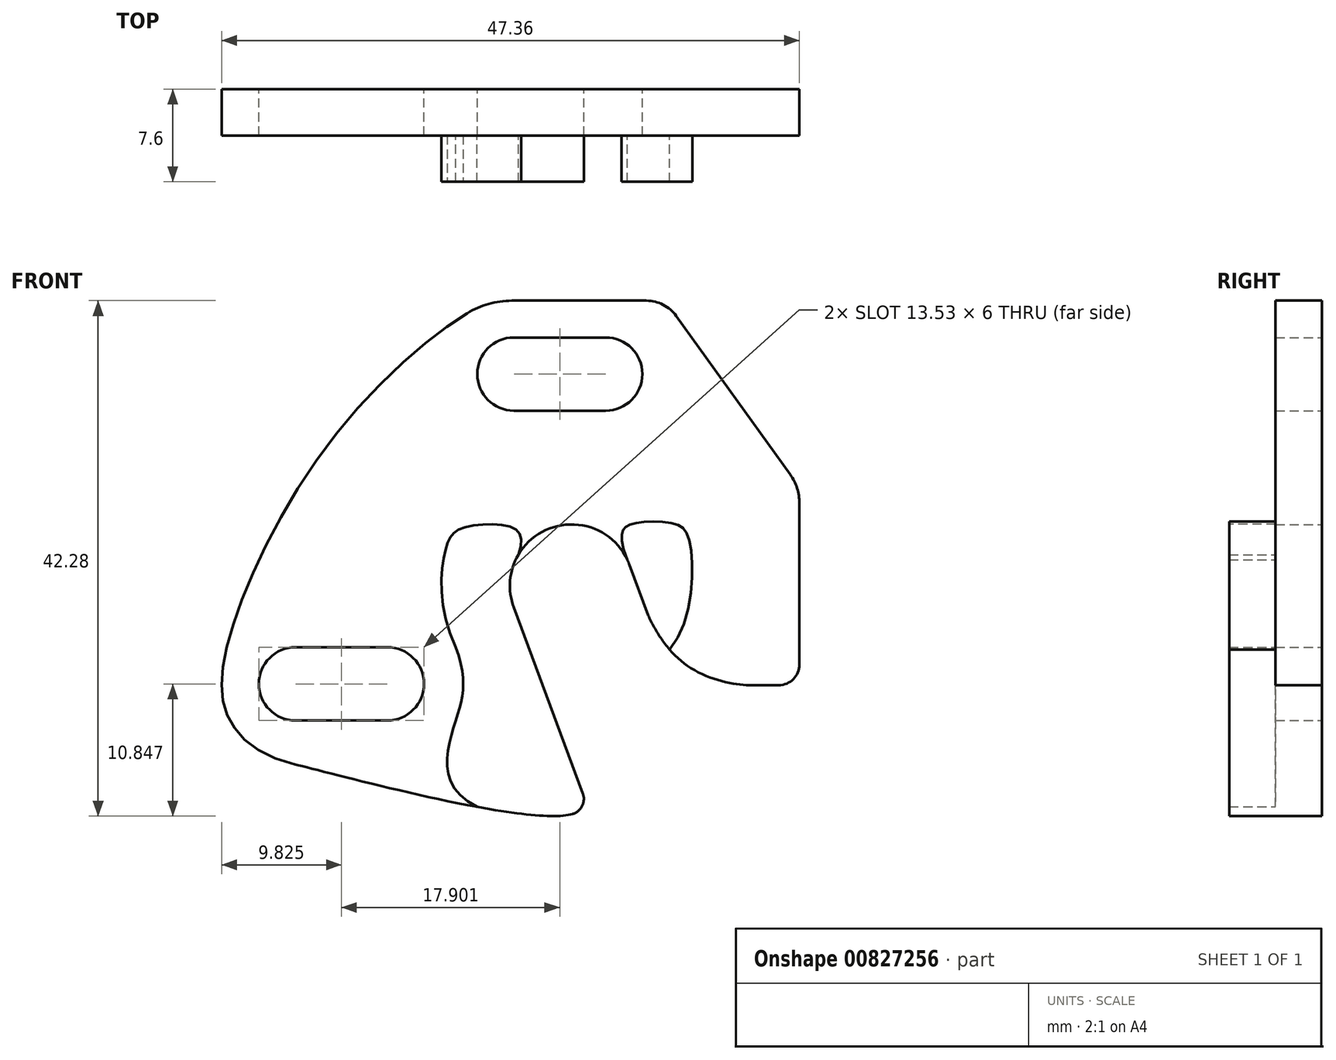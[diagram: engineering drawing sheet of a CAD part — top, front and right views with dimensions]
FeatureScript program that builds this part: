
annotation { "Feature Type Name" : "Feature", "Feature Type Description" : "" }
export const myFeature = defineFeature(function(context is Context, id is Id, definition is map)
    precondition{}
    {
        {
            var Q0;
            Q0=qCreatedBy(makeId("Front.planeOp"),FACE);
            var sketch = newSketch(context, id + "F0", { "sketchPlane" : qUnion([Q0])});
            skLineSegment(sketch, "E0", {"start": v(8.14, 19.75) * mm, "end": v(-6.15, 19.75) * mm});
            skLineSegment(sketch, "E1", {"start": v(8.14, 19.75) * mm, "end": v(19.14, 4.43) * mm});
            skLineSegment(sketch, "E2", {"start": v(19.14, 4.43) * mm, "end": v(19.14, -11.79) * mm});
            skFitSpline(sketch, "E3", {"points": [v(-6.15, 19.75) * mm, v(-18.96, 8.66) * mm, v(-27.78, -8.68) * mm, v(-27.55, -14.68) * mm, v(-22.16, -18.3) * mm], "startDerivative": vector(-32.4, -14.02) * mm, "endDerivative": vector(43.77, -10.22) * mm});
            skFitSpline(sketch, "E4", {"points": [v(-22.16, -18.3) * mm, v(0.53, -22.37) * mm], "startDerivative": vector(8.15, -1.9) * mm, "endDerivative": vector(11.4, 3.19) * mm});
            skLineSegment(sketch, "E5", {"start": v(1.4, -20.68) * mm, "end": v(-4.27, -5.41) * mm});
            skLineSegment(sketch, "E6", {"start": v(6.75, -6.07) * mm, "end": v(5.2, -1.9) * mm});
            skLineSegment(sketch, "E7", {"start": v(19.14, -11.79) * mm, "end": v(15.04, -11.79) * mm});
            skFitSpline(sketch, "E8", {"points": [v(6.75, -6.07) * mm, v(10.01, -10.24) * mm, v(15.04, -11.79) * mm], "startDerivative": vector(3.92, -8.46) * mm, "endDerivative": vector(7.84, 0) * mm});
            skLineSegment(sketch, "E9", {"start": v(3.27, 10.73) * mm, "end": v(-4.26, 10.73) * mm});
            skLineSegment(sketch, "E10", {"start": v(-4.26, 16.73) * mm, "end": v(3.27, 16.73) * mm});
            skLineSegment(sketch, "E11", {"start": v(-22.16, -8.68) * mm, "end": v(-14.63, -8.68) * mm});
            skLineSegment(sketch, "E12", {"start": v(-22.16, -14.68) * mm, "end": v(-14.63, -14.68) * mm});
            skArc(sketch, "E13", {"start": v(-22.16, -8.68) * mm, "mid": v(-25.16, -11.68) * mm, "end": v(-22.16, -14.68) * mm});
            skArc(sketch, "E14", {"start": v(-14.63, -14.68) * mm, "mid": v(-11.63, -11.68) * mm, "end": v(-14.63, -8.68) * mm});
            skArc(sketch, "E15", {"start": v(-4.26, 16.73) * mm, "mid": v(-7.26, 13.73) * mm, "end": v(-4.26, 10.73) * mm});
            skArc(sketch, "E16", {"start": v(3.27, 10.73) * mm, "mid": v(6.27, 13.73) * mm, "end": v(3.27, 16.73) * mm});
            skPoint(sketch, "E17", {"position": v(-7.27, -21.78) * mm});
            skFitSpline(sketch, "E18", {"points": [v(-7.27, -21.78) * mm, v(-9.02, -14.68) * mm, v(-9.02, -8.68) * mm], "startDerivative": vector(-19.93, 9.83) * mm, "endDerivative": vector(-6.24, 17.1) * mm});
            skFitSpline(sketch, "E19", {"points": [v(-9.02, -8.68) * mm, v(-9.78, -0.39) * mm, v(-8.5, 1.08) * mm, v(-4.25, 1.07) * mm, v(-3.9, -1.1) * mm], "startDerivative": vector(-12.99, 27.31) * mm, "endDerivative": vector(-6.01, -17.5) * mm});
            skFitSpline(sketch, "E20", {"points": [v(8.5, -8.87) * mm, v(10.14, 0) * mm, v(8.95, 1.43) * mm, v(5.63, 1.49) * mm, v(4.7, 0.94) * mm, v(5.2, -1.9) * mm], "startDerivative": vector(17.97, 20.2) * mm, "endDerivative": vector(11.04, -25.23) * mm});
            skArc(sketch, "E21", {"start": v(0.53, -22.37) * mm, "mid": v(1.33, -21.71) * mm, "end": v(1.4, -20.68) * mm});
            skArc(sketch, "E22", {"start": v(5.2, -1.9) * mm, "mid": v(-1.3, 1.08) * mm, "end": v(-4.27, -5.41) * mm});
            skSolve(sketch);
        }
        {
            var Q0;
            Q0=makeQuery(id+"F0.imprint","IMPRINT",FACE,{"disambiguationData":[TD([[makeQuery(id+"F0.imprint","IMPRINT",EDGE,{"derivedFrom":sQuery(id+"F0.wireOp",EDGE,"E0")}),1.0]])]});
            extrude(context, id + "F1", {"entities" : qUnion([Q0]), "depth" : 3.8 * mm, "offsetDistance" : 25 * mm});
        }
        {
            var Q0;
            {var subQ1=sQuery(id+"F0.wireOp",EDGE,"E5");Q0=makeQuery(id+"F0.imprint","IMPRINT",FACE,{"disambiguationData":[TD([[makeQuery(id+"F0.imprint","IMPRINT",EDGE,{"derivedFrom":subQ1}),1.0]])]});}
            var Q1;
            {var subQ0=sQuery(id+"F0.wireOp",EDGE,"E6");Q1=makeQuery(id+"F0.imprint","IMPRINT",FACE,{"disambiguationData":[TD([[makeQuery(id+"F0.imprint","IMPRINT",EDGE,{"derivedFrom":subQ0}),-1.0]])]});}
            extrude(context, id + "F2", {"entities" : qUnion([Q0, Q1]), "operationType" : NewBodyOperationType.ADD, "depth" : 7.6 * mm, "offsetDistance" : 25 * mm});
        }
        {
            var Q0;
            Q0=makeQuery(id+"F1.opExtrude","SWEPT_EDGE",EDGE,{"disambiguationData":[OSD([sQuery(id+"F0.wireOp",EDGE,"E0"),sQuery(id+"F0.wireOp",EDGE,"E3")])]});
            fillet(context, id + "F3", {"entities" : qUnion([Q0]), "radius" : 7 * mm, "tangentPropagation" : true, "allowEdgeOverflow" : false});
        }
        {
            var Q0;
            Q0=makeQuery(id+"F1.opExtrude","SWEPT_EDGE",EDGE,{"disambiguationData":[OSD([sQuery(id+"F0.wireOp",EDGE,"E0"),sQuery(id+"F0.wireOp",EDGE,"E1")])]});
            fillet(context, id + "F4", {"entities" : qUnion([Q0]), "radius" : 3 * mm, "tangentPropagation" : true, "allowEdgeOverflow" : false});
        }
        {
            var Q0;
            Q0=makeQuery(id+"F1.opExtrude","SWEPT_EDGE",EDGE,{"disambiguationData":[OSD([sQuery(id+"F0.wireOp",EDGE,"E1"),sQuery(id+"F0.wireOp",EDGE,"E2")])]});
            fillet(context, id + "F5", {"entities" : qUnion([Q0]), "radius" : 4 * mm, "tangentPropagation" : true, "allowEdgeOverflow" : false});
        }
        {
            var Q0;
            Q0=makeQuery(id+"F1.opExtrude","SWEPT_EDGE",EDGE,{"disambiguationData":[OSD([sQuery(id+"F0.wireOp",EDGE,"E2"),sQuery(id+"F0.wireOp",EDGE,"E7")])]});
            fillet(context, id + "F6", {"entities" : qUnion([Q0]), "radius" : 1.7 * mm, "tangentPropagation" : true, "allowEdgeOverflow" : false});
        }
    });
